# Revit family: Cypher-C2
name_source: partatom
category: Lighting Fixtures
units: mm (PartAtom-declared; Revit-internal decimal feet)

## family parameters
Always vertical = Yes
Cut with Voids When Loaded = No
Host = Wall
Light Source = Yes
OmniClass Number = 23.80.70.11.14
OmniClass Title = General Luminaries, Directional
Part Type = Normal
Room Calculation Point = No
Round Connector Dimension = Use Diameter
Shared = No

## types (6) — shared parameters
120 Voltage = Yes
277 Voltage = No
Assembly Code = D5020
Box Finish = White
Color Filter = 16777215
Description = Cypher allows designers to mix and match optics for best-in-class aesthetics and performance
Dimming Lamp Color Temperature Shift = <None>
Emit Shape Visible in Rendering = No
Emit from Rectangle Length = 3 "
Emit from Rectangle Width = 9 "
Glass = White Glass
Lamp = 360° Light Distribution
Load Classification = Lighting
Manufacturer = Architectural Area Lighting
Model = Cypher - Pedestrian Scale
Photometric Notes = More IES files download Photometric Web Link
Power Factor = 1
Tilt Angle = 90.00°
URL = https://www.currentlighting.com
Voltage = 120 V
zero-valued in all types: Default Elevation

## per-type parameters (varying)
| type | Apparent Load | Photometric Web File | Wattage Comments | Watts |
| CY2-25-3K7-1-2-R | 26 VA | CY2-25-3K7-1-2-R.ies | 25W, 2500 nominal lumens | 26 W |
| CY2-25-4K7-1-SP-R | 26 VA | CY2-25-4K7-1-SP-R.IES | 25W, 2500 nominal lumens | 26 W |
| CY2-35-4K7-1-1D-R | 40 VA | CY2-35-4K7-1-1D-R.ies | 40W, 3500 nominal lumens | 40 W |
| CY2-35-5K7-1-WG-R | 40 VA | CY2-35-5K7-1-WG-R.IES | 40W, 3500 nominal lumens | 40 W |
| CY2-45-3K7-1-3-R | 52 VA | CY2-45-3K7-1-3-R.IES | 50W, 4500 nominal lumens | 52 W |
| CY2-45-5K7-1-4D-R | 52 VA | CY2-45-5K7-1-4D-R.IES | 50W, 4500 nominal lumens | 52 W |

## geometry (parser evidence)
native form markers: Blend x28, Sweep x3
no freeform markers — native parametric forms only
